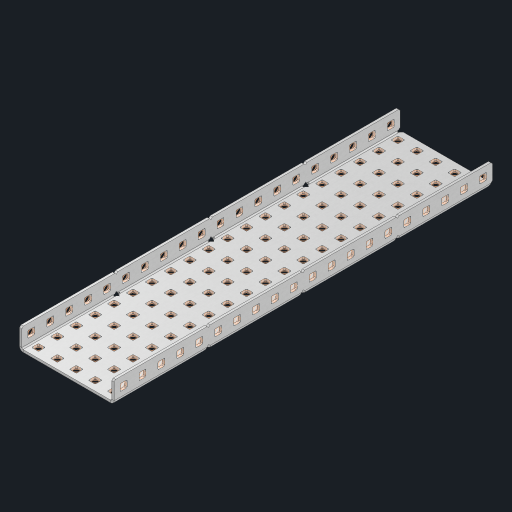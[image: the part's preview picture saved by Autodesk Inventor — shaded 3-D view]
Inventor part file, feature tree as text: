
AUTODESK INVENTOR PART (.ipt)
format: ipt  version: 2023 (Build 270158000, 158)  size: 1,668,608 bytes
history: native  units: in
note: dims shown in document units (in); Inventor stores cm internally (conversion verified against a paired STEP export)
features: other x145, extrude x139, sheet_metal_op x10, sketch x8, mirror x1, pattern_linear x1, chamfer x1
ambient origin geometry x8: Origin, YZ Plane, XZ Plane, XY Plane, X Axis, Y Axis, Z Axis, Center Point
bodies: Solid1 (feature_tree), Body (feature_tree)
feature tree (305):
  other  "Flange Pattern Plane"
  sheet_metal_op  "Flange Pattern"
  sheet_metal_op  "Body Pattern"
  other  "Arc Length"
  mirror  "Notch Mirror"
  pattern_linear  "Notch Pattern"  Spacing1=0.25in  [1 undecoded]
  chamfer  "End Chamfer"
  extrude  "Half Cut"  Depth=0.0625in
  sketch  "Sketch1"  dims[d0=2.5in]
  other  "Plate1"
  sketch  "Sketch2"  dims[d1=10.0in]
  other  "Plate2"
  sheet_metal_op  "Bend1"
  sheet_metal_op  "Corner1"
  sketch  "Sketch3"  dims[d2=0.0625in]
  other  "Flange Pattern Sketch"
  sketch  "Sketch7"  dims[d3=0.0625in]
  other  "Srf1"
  other  "Srf2"
  sketch  "Sketch8"  dims[d4=0.0312in]
  sketch  "Sketch9"  dims[d5=0.125in]
  other  "Srf91"
  sheet_metal_op  "Body Pattern Sketch"
  other  "Srf92"
  sketch  "Sketch13"  dims[d6=0.0625in]
  sketch  "Sketch14"  dims[d7=0.5in d8=90.0deg d9=0.0312in d10=0.25in d11=0.0625in d12=0.0625in d16=0.182in d17=0.02in d18=0.0625in d19=0.0in d20=0.25in d21=0.25in d46=0.172in d47=1.0in d48=0.0in d49=0.182in d50=0.02in d51=0.25in d52=0.25in d53=0.0625in d54=0.0in d55=0.172in d56=1.0in d57=0.0in d60=7.874in d62=0.5in d63=1.9685in d65=0.5in d85=0.1473in d86=0.1782in d88=0.04in d89=0.0625in d90=0.0in d91=0.04in d92=0.0491in d95=2.5in d96=0.04in d97=0.25in d98=45.0deg d101=0.0in d102=2.497in d131=2.5in d132=7.874in d134=0.5in d139=0.5in]
  other  "Srf856"
  other  "Srf1310"
  other  "Srf1311"
  other  "Srf1312"
  other  "Srf1376"
  other  "Srf1377"
  other  "Srf1728"
  other  "Srf1755"
  other  "Srf1878"
  other  "Srf1879"
  other  "Srf1880"
  other  "Srf1881"
  other  "Srf1882"
  other  "Srf1883"
  other  "Srf1884"
  other  "Srf1885"
  other  "Srf1886"
  other  "Srf1887"
  other  "Srf1888"
  other  "Srf1889"
  other  "Srf1890"
  other  "Srf1891"
  other  "Srf1892"
  other  "Srf1893"
  other  "Srf1894"
  other  "Srf1895"
  other  "Srf1896"
  other  "Srf1897"
  other  "Srf1898"
  other  "Srf1899"
  other  "Srf1900"
  other  "Srf1901"
  other  "Srf1902"
  other  "Srf1903"
  other  "Srf1904"
  other  "Srf1905"
  other  "Srf1906"
  other  "Srf1942"
  other  "Srf1943"
  other  "Srf1944"
  other  "Srf1945"
  other  "Srf1946"
  other  "Srf1947"
  other  "Srf1948"
  other  "Srf1949"
  other  "Srf1950"
  other  "Srf1951"
  other  "Srf1952"
  other  "Srf1953"
  other  "Srf1954"
  other  "Srf1955"
  other  "Srf1956"
  other  "Srf1957"
  other  "Srf1958"
  other  "Srf1959"
  other  "Srf1960"
  other  "Srf1961"
  other  "Srf1962"
  other  "Srf1963"
  other  "Srf1964"
  other  "Srf1965"
  other  "Srf1966"
  other  "Srf1967"
  other  "Srf1968"
  other  "Srf1969"
  other  "Srf1970"
  other  "Srf2111"
  other  "Srf2112"
  other  "Srf2113"
  other  "Srf2114"
  other  "Srf2115"
  other  "Srf2146"
  other  "Srf2147"
  other  "Srf2148"
  other  "Srf2149"
  other  "Srf2150"
  other  "Srf2151"
  other  "Srf2152"
  other  "Srf2153"
  other  "Srf2154"
  other  "Srf2155"
  other  "Srf2156"
  other  "Srf2157"
  other  "Srf2158"
  other  "Srf2159"
  other  "Srf2160"
  other  "Srf2161"
  other  "Srf2162"
  other  "Srf2163"
  other  "Srf2164"
  other  "Srf2165"
  other  "Srf2166"
  other  "Srf2167"
  other  "Srf2168"
  other  "Srf2169"
  other  "Srf2170"
  other  "Srf2171"
  other  "Srf2172"
  other  "Srf2173"
  other  "Srf2174"
  other  "Srf2175"
  other  "Srf2176"
  other  "Srf2177"
  other  "Srf2178"
  other  "Srf2179"
  other  "Srf2180"
  other  "Srf2181"
  other  "Srf2182"
  other  "Srf2183"
  other  "Srf2184"
  other  "Srf2185"
  other  "Srf2186"
  other  "Srf2187"
  other  "Srf2188"
  other  "Srf2189"
  other  "Srf2190"
  other  "Srf2191"
  other  "Srf2192"
  other  "Srf2193"
  other  "Srf2194"
  other  "Srf2195"
  other  "Srf2196"
  other  "Srf2197"
  other  "Srf2198"
  other  "Srf2199"
  other  "Srf2200"
  other  "Srf2201"
  other  "Srf2202"
  other  "Srf2203"
  other  "Srf2204"
  other  "Srf2205"
  other  "Srf2206"
  other  "Srf2207"
  other  "Srf2208"
  other  "Srf2209"
  other  "Srf2210"
  sheet_metal_op  "Flange Stamp"
  sheet_metal_op  "Flange Circle"
  sheet_metal_op  "Body Stamp"
  sheet_metal_op  "Body Circle"
  sheet_metal_op  "Notch"
  extrude  "ExtrusionSrf2"  Depth=0.0625in
  extrude  "ExtrusionSrf92"  Depth=2.5in
  extrude  "ExtrusionSrf856"  Depth=0.02in
  extrude  "ExtrusionSrf1310"  Depth=0.0625in
  extrude  "ExtrusionSrf1311"  TaperAngle=0.0deg  [1 undecoded]
  extrude  "ExtrusionSrf1312"  Depth=0.25in
  extrude  "ExtrusionSrf1376"  Depth=0.25in
  extrude  "ExtrusionSrf1377"  Depth=2.5in
  extrude  "ExtrusionSrf1728"  Depth=2.5in TaperAngle=0.0deg
  extrude  "ExtrusionSrf1755"  Depth=2.5in
  extrude  "ExtrusionSrf1878"  Depth=0.02in
  extrude  "ExtrusionSrf1879"  Depth=0.25in
  extrude  "ExtrusionSrf1880"  Depth=0.25in
  extrude  "ExtrusionSrf1881"  Depth=0.0625in
  extrude  "ExtrusionSrf1882"  TaperAngle=0.0deg  [1 undecoded]
  extrude  "ExtrusionSrf1883"  Depth=2.5in
  extrude  "ExtrusionSrf1884"  Depth=2.5in TaperAngle=0.0deg
  extrude  "ExtrusionSrf1885"  Depth=2.5in
  extrude  "ExtrusionSrf1886"  Depth=2.5in
  extrude  "ExtrusionSrf1887"  Depth=2.5in
  extrude  "ExtrusionSrf1888"  Depth=2.5in
  extrude  "ExtrusionSrf1889"  Depth=2.5in
  extrude  "ExtrusionSrf1890"  Depth=0.0625in
  extrude  "ExtrusionSrf1891"  TaperAngle=0.0deg  [1 undecoded]
  extrude  "ExtrusionSrf1892"  Depth=2.5in
  extrude  "ExtrusionSrf1893"  Depth=2.5in
  extrude  "ExtrusionSrf1894"  Depth=2.5in
  extrude  "ExtrusionSrf1895"  Depth=0.25in TaperAngle=45.0deg
  extrude  "ExtrusionSrf1896"  TaperAngle=0.0deg  [1 undecoded]
  extrude  "ExtrusionSrf1897"  Depth=2.5in
  extrude  "ExtrusionSrf1898"  Depth=2.5in
  extrude  "ExtrusionSrf1899"  Depth=2.5in
  extrude  "ExtrusionSrf1900"  Depth=2.5in
  extrude  "ExtrusionSrf1901"  Depth=2.5in
  extrude  "ExtrusionSrf1902"  [1 undecoded]
  extrude  "ExtrusionSrf1903"  [1 undecoded]
  extrude  "ExtrusionSrf1904"  [1 undecoded]
  extrude  "ExtrusionSrf1905"  [1 undecoded]
  extrude  "ExtrusionSrf1906"  [1 undecoded]
  extrude  "ExtrusionSrf1942"  [1 undecoded]
  extrude  "ExtrusionSrf1943"  [1 undecoded]
  extrude  "ExtrusionSrf1944"  [1 undecoded]
  extrude  "ExtrusionSrf1945"  [1 undecoded]
  extrude  "ExtrusionSrf1946"  [1 undecoded]
  extrude  "ExtrusionSrf1947"  [1 undecoded]
  extrude  "ExtrusionSrf1948"  [1 undecoded]
  extrude  "ExtrusionSrf1949"  [1 undecoded]
  extrude  "ExtrusionSrf1950"  [1 undecoded]
  extrude  "ExtrusionSrf1951"  [1 undecoded]
  extrude  "ExtrusionSrf1952"  [1 undecoded]
  extrude  "ExtrusionSrf1953"  [1 undecoded]
  extrude  "ExtrusionSrf1954"  [1 undecoded]
  extrude  "ExtrusionSrf1955"  [1 undecoded]
  extrude  "ExtrusionSrf1956"  [1 undecoded]
  extrude  "ExtrusionSrf1957"  [1 undecoded]
  extrude  "ExtrusionSrf1958"  [1 undecoded]
  extrude  "ExtrusionSrf1959"  [1 undecoded]
  extrude  "ExtrusionSrf1960"  [1 undecoded]
  extrude  "ExtrusionSrf1961"  [1 undecoded]
  extrude  "ExtrusionSrf1962"  [1 undecoded]
  extrude  "ExtrusionSrf1963"  [1 undecoded]
  extrude  "ExtrusionSrf1964"  [1 undecoded]
  extrude  "ExtrusionSrf1965"  [1 undecoded]
  extrude  "ExtrusionSrf1966"  [1 undecoded]
  extrude  "ExtrusionSrf1967"  [1 undecoded]
  extrude  "ExtrusionSrf1968"  [1 undecoded]
  extrude  "ExtrusionSrf1969"  [1 undecoded]
  extrude  "ExtrusionSrf1970"  [1 undecoded]
  extrude  "ExtrusionSrf2111"  [1 undecoded]
  extrude  "ExtrusionSrf2112"  [1 undecoded]
  extrude  "ExtrusionSrf2113"  [1 undecoded]
  extrude  "ExtrusionSrf2114"  [1 undecoded]
  extrude  "ExtrusionSrf2115"  [1 undecoded]
  extrude  "ExtrusionSrf2146"  [1 undecoded]
  extrude  "ExtrusionSrf2147"  [1 undecoded]
  extrude  "ExtrusionSrf2148"  [1 undecoded]
  extrude  "ExtrusionSrf2149"  [1 undecoded]
  extrude  "ExtrusionSrf2150"  [1 undecoded]
  extrude  "ExtrusionSrf2151"  [1 undecoded]
  extrude  "ExtrusionSrf2152"  [1 undecoded]
  extrude  "ExtrusionSrf2153"  [1 undecoded]
  extrude  "ExtrusionSrf2154"  [1 undecoded]
  extrude  "ExtrusionSrf2155"  [1 undecoded]
  extrude  "ExtrusionSrf2156"  [1 undecoded]
  extrude  "ExtrusionSrf2157"  [1 undecoded]
  extrude  "ExtrusionSrf2158"  [1 undecoded]
  extrude  "ExtrusionSrf2159"  [1 undecoded]
  extrude  "ExtrusionSrf2160"  [1 undecoded]
  extrude  "ExtrusionSrf2161"  [1 undecoded]
  extrude  "ExtrusionSrf2162"  [1 undecoded]
  extrude  "ExtrusionSrf2163"  [1 undecoded]
  extrude  "ExtrusionSrf2164"  [1 undecoded]
  extrude  "ExtrusionSrf2165"  [1 undecoded]
  extrude  "ExtrusionSrf2166"  [1 undecoded]
  extrude  "ExtrusionSrf2167"  [1 undecoded]
  extrude  "ExtrusionSrf2168"  [1 undecoded]
  extrude  "ExtrusionSrf2169"  [1 undecoded]
  extrude  "ExtrusionSrf2170"  [1 undecoded]
  extrude  "ExtrusionSrf2171"  [1 undecoded]
  extrude  "ExtrusionSrf2172"  [1 undecoded]
  extrude  "ExtrusionSrf2173"  [1 undecoded]
  extrude  "ExtrusionSrf2174"  [1 undecoded]
  extrude  "ExtrusionSrf2175"  [1 undecoded]
  extrude  "ExtrusionSrf2176"  [1 undecoded]
  extrude  "ExtrusionSrf2177"  [1 undecoded]
  extrude  "ExtrusionSrf2178"  [1 undecoded]
  extrude  "ExtrusionSrf2179"  [1 undecoded]
  extrude  "ExtrusionSrf2180"  [1 undecoded]
  extrude  "ExtrusionSrf2181"  [1 undecoded]
  extrude  "ExtrusionSrf2182"  [1 undecoded]
  extrude  "ExtrusionSrf2183"  [1 undecoded]
  extrude  "ExtrusionSrf2184"  [1 undecoded]
  extrude  "ExtrusionSrf2185"  [1 undecoded]
  extrude  "ExtrusionSrf2186"  [1 undecoded]
  extrude  "ExtrusionSrf2187"  [1 undecoded]
  extrude  "ExtrusionSrf2188"  [1 undecoded]
  extrude  "ExtrusionSrf2189"  [1 undecoded]
  extrude  "ExtrusionSrf2190"  [1 undecoded]
  extrude  "ExtrusionSrf2191"  [1 undecoded]
  extrude  "ExtrusionSrf2192"  [1 undecoded]
  extrude  "ExtrusionSrf2193"  [1 undecoded]
  extrude  "ExtrusionSrf2194"  [1 undecoded]
  extrude  "ExtrusionSrf2195"  [1 undecoded]
  extrude  "ExtrusionSrf2196"  [1 undecoded]
  extrude  "ExtrusionSrf2197"  [1 undecoded]
  extrude  "ExtrusionSrf2198"  [1 undecoded]
  extrude  "ExtrusionSrf2199"  [1 undecoded]
  extrude  "ExtrusionSrf2200"  [1 undecoded]
  extrude  "ExtrusionSrf2201"  [1 undecoded]
  extrude  "ExtrusionSrf2202"  [1 undecoded]
  extrude  "ExtrusionSrf2203"  [1 undecoded]
  extrude  "ExtrusionSrf2204"  [1 undecoded]
  extrude  "ExtrusionSrf2205"  [1 undecoded]
  extrude  "ExtrusionSrf2206"  [1 undecoded]
  extrude  "ExtrusionSrf2207"  [1 undecoded]
  extrude  "ExtrusionSrf2208"  [1 undecoded]
  extrude  "ExtrusionSrf2209"  [1 undecoded]
  extrude  "ExtrusionSrf2210"  [1 undecoded]
note: 109 required parameter values undecoded (feature->parameter linkage not recoverable at this tier; creation-order binding heuristic only, values carry confidence <= 0.55)
